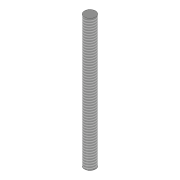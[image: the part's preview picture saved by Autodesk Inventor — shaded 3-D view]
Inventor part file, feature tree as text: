
AUTODESK INVENTOR PART (.ipt)
format: ipt  version: 2020 (Build 240168000, 168)  size: 76,288 bytes
history: native  units: in
note: dims shown in document units (in); Inventor stores cm internally (conversion verified against a paired STEP export)
features: extrude x1, thread x1, sketch x1
ambient origin geometry x8: Origin, YZ Plane, XZ Plane, XY Plane, X Axis, Y Axis, Z Axis, Center Point
bodies: Solid1 (feature_tree)
feature tree (3):
  extrude  "Extrusion1"  Depth=2.3622in TaperAngle=0.0deg
  thread  "Thread1"  [1 undecoded]
  sketch  "Sketch1"  dims[d0=0.1969in d1=2.3622in d2=0.0in d3=2.362in d4=0.0in]
note: 1 required parameter value undecoded (feature->parameter linkage not recoverable at this tier; creation-order binding heuristic only, values carry confidence <= 0.55)
